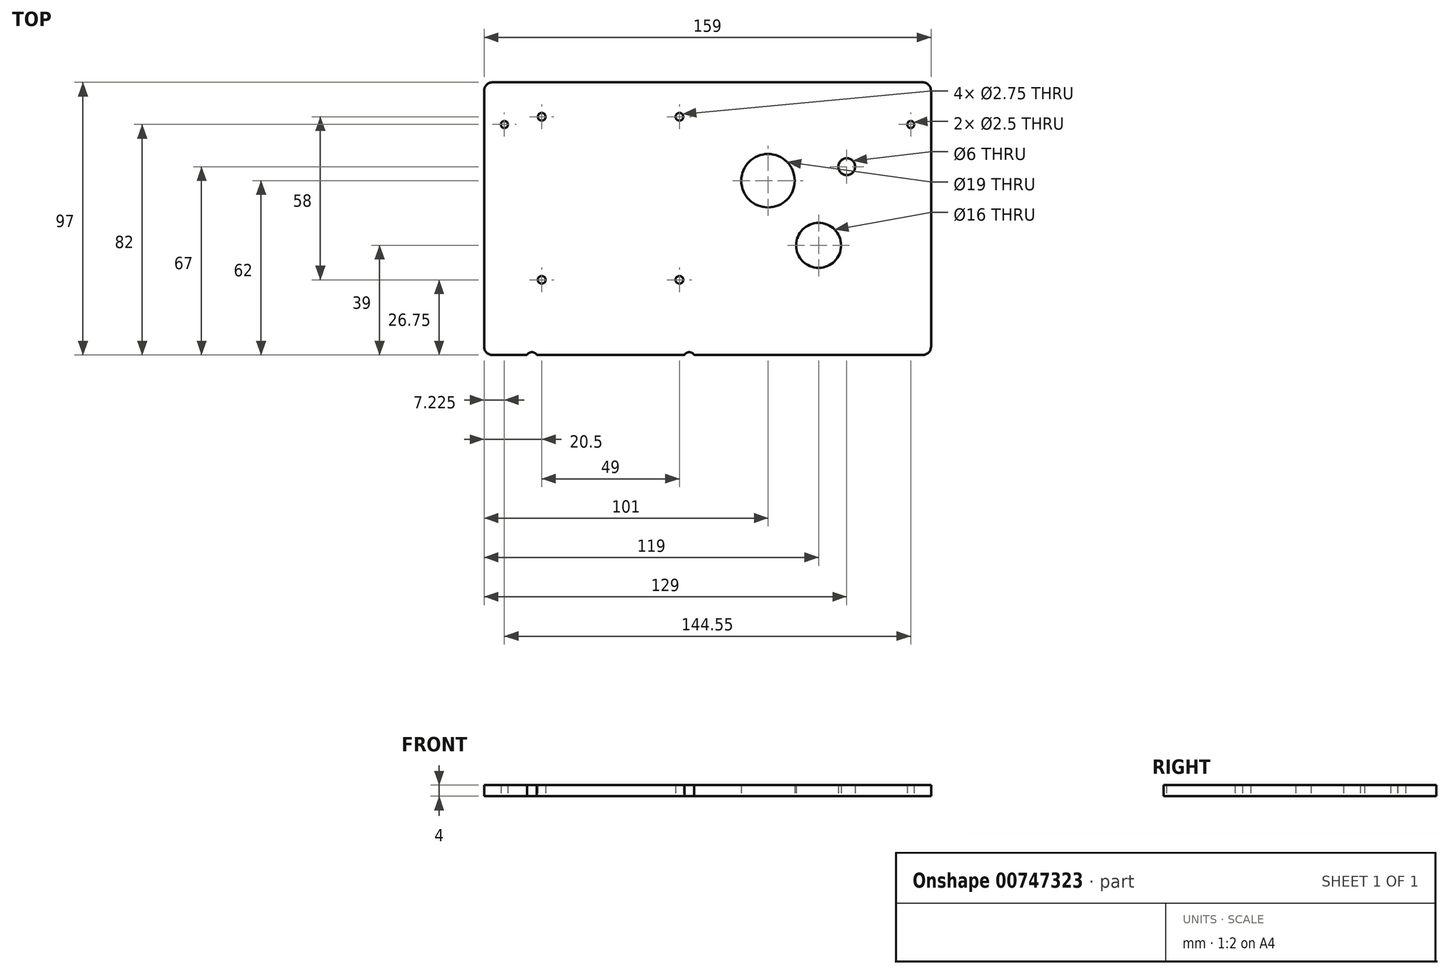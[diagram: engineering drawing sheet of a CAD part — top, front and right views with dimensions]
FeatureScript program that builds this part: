
annotation { "Feature Type Name" : "Feature", "Feature Type Description" : "" }
export const myFeature = defineFeature(function(context is Context, id is Id, definition is map)
    precondition{}
    {
        {
            var Q0;
            Q0=qCreatedBy(makeId("Top.planeOp"),FACE);
            var sketch = newSketch(context, id + "F0", { "sketchPlane" : qUnion([Q0])});
            skLineSegment(sketch, "E0.bottom", {"start": v(79.5, -48.5) * mm, "end": v(-79.5, -48.5) * mm});
            skLineSegment(sketch, "E0.top", {"start": v(79.5, 48.5) * mm, "end": v(-79.5, 48.5) * mm});
            skLineSegment(sketch, "E0.left", {"start": v(79.5, -48.5) * mm, "end": v(79.5, 48.5) * mm});
            skLineSegment(sketch, "E0.right", {"start": v(-79.5, -48.5) * mm, "end": v(-79.5, 48.5) * mm});
            skPoint(sketch, "E0.middle", {"position": v(0, 0) * mm});
            skLineSegment(sketch, "E1.bottom", {"start": v(-79.5, -48.5) * mm, "end": v(79.5, -48.5) * mm});
            skLineSegment(sketch, "E1.top", {"start": v(-79.5, -90.5) * mm, "end": v(79.5, -90.5) * mm});
            skLineSegment(sketch, "E1.left", {"start": v(-79.5, -48.5) * mm, "end": v(-79.5, -90.5) * mm});
            skLineSegment(sketch, "E1.right", {"start": v(79.5, -48.5) * mm, "end": v(79.5, -90.5) * mm});
            skLineSegment(sketch, "E2.bottom", {"start": v(-79.5, 48.5) * mm, "end": v(-72.28, 48.5) * mm, "construction": true});
            skLineSegment(sketch, "E2.top", {"start": v(-79.5, 33.5) * mm, "end": v(-72.28, 33.5) * mm, "construction": true});
            skLineSegment(sketch, "E2.left", {"start": v(-79.5, 48.5) * mm, "end": v(-79.5, 33.5) * mm, "construction": true});
            skLineSegment(sketch, "E2.right", {"start": v(-72.28, 48.5) * mm, "end": v(-72.28, 33.5) * mm, "construction": true});
            skLineSegment(sketch, "E3.bottom", {"start": v(79.5, 48.5) * mm, "end": v(72.28, 48.5) * mm, "construction": true});
            skLineSegment(sketch, "E3.top", {"start": v(79.5, 33.5) * mm, "end": v(72.28, 33.5) * mm, "construction": true});
            skLineSegment(sketch, "E3.left", {"start": v(79.5, 48.5) * mm, "end": v(79.5, 33.5) * mm, "construction": true});
            skLineSegment(sketch, "E3.right", {"start": v(72.28, 48.5) * mm, "end": v(72.28, 33.5) * mm, "construction": true});
            skCircle(sketch, "E4", {"center": v(-72.28, 33.5) * mm, "radius": 1.25 * mm});
            skCircle(sketch, "E5", {"center": v(72.28, 33.5) * mm, "radius": 1.25 * mm});
            skLineSegment(sketch, "E6.bottom", {"start": v(-62.5, -90.5) * mm, "end": v(-6.5, -90.5) * mm});
            skLineSegment(sketch, "E6.top", {"start": v(-62.5, -49.5) * mm, "end": v(-6.5, -49.5) * mm});
            skLineSegment(sketch, "E6.left", {"start": v(-62.5, -90.5) * mm, "end": v(-62.5, -49.5) * mm});
            skLineSegment(sketch, "E6.right", {"start": v(-6.5, -90.5) * mm, "end": v(-6.5, -49.5) * mm});
            skCircle(sketch, "E7", {"center": v(-62.5, -49.5) * mm, "radius": 2 * mm});
            skCircle(sketch, "E8", {"center": v(-6.5, -49.5) * mm, "radius": 2 * mm});
            skLineSegment(sketch, "E9.bottom", {"start": v(-79.5, -90.5) * mm, "end": v(-72.4, -90.5) * mm, "construction": true});
            skLineSegment(sketch, "E9.top", {"start": v(-79.5, -63.95) * mm, "end": v(-72.4, -63.95) * mm, "construction": true});
            skLineSegment(sketch, "E9.left", {"start": v(-79.5, -90.5) * mm, "end": v(-79.5, -63.95) * mm, "construction": true});
            skLineSegment(sketch, "E9.right", {"start": v(-72.4, -90.5) * mm, "end": v(-72.4, -63.95) * mm, "construction": true});
            skLineSegment(sketch, "E10.bottom", {"start": v(79.5, -90.5) * mm, "end": v(72.4, -90.5) * mm, "construction": true});
            skLineSegment(sketch, "E10.top", {"start": v(79.5, -63.95) * mm, "end": v(72.4, -63.95) * mm, "construction": true});
            skLineSegment(sketch, "E10.left", {"start": v(79.5, -90.5) * mm, "end": v(79.5, -63.95) * mm, "construction": true});
            skLineSegment(sketch, "E10.right", {"start": v(72.4, -90.5) * mm, "end": v(72.4, -63.95) * mm, "construction": true});
            skCircle(sketch, "E11", {"center": v(-72.4, -63.95) * mm, "radius": 1.25 * mm});
            skCircle(sketch, "E12", {"center": v(72.4, -63.95) * mm, "radius": 1.25 * mm});
            skLineSegment(sketch, "E13.bottom", {"start": v(-79.5, 48.5) * mm, "end": v(-62.5, 48.5) * mm, "construction": true});
            skLineSegment(sketch, "E13.top", {"start": v(-79.5, 39.75) * mm, "end": v(-62.5, 39.75) * mm, "construction": true});
            skLineSegment(sketch, "E13.left", {"start": v(-79.5, 48.5) * mm, "end": v(-79.5, 39.75) * mm, "construction": true});
            skLineSegment(sketch, "E13.right", {"start": v(-62.5, 48.5) * mm, "end": v(-62.5, 39.75) * mm, "construction": true});
            skLineSegment(sketch, "E14.bottom", {"start": v(-62.5, 39.75) * mm, "end": v(-6.5, 39.75) * mm, "construction": true});
            skLineSegment(sketch, "E14.top", {"start": v(-62.5, -45.25) * mm, "end": v(-6.5, -45.25) * mm, "construction": true});
            skLineSegment(sketch, "E14.left", {"start": v(-62.5, 39.75) * mm, "end": v(-62.5, -45.25) * mm, "construction": true});
            skLineSegment(sketch, "E14.right", {"start": v(-6.5, 39.75) * mm, "end": v(-6.5, -45.25) * mm, "construction": true});
            skLineSegment(sketch, "E15.bottom", {"start": v(-62.5, 39.75) * mm, "end": v(-59, 39.75) * mm, "construction": true});
            skLineSegment(sketch, "E15.top", {"start": v(-62.5, 36.25) * mm, "end": v(-59, 36.25) * mm, "construction": true});
            skLineSegment(sketch, "E15.left", {"start": v(-62.5, 39.75) * mm, "end": v(-62.5, 36.25) * mm, "construction": true});
            skLineSegment(sketch, "E15.right", {"start": v(-59, 39.75) * mm, "end": v(-59, 36.25) * mm, "construction": true});
            skLineSegment(sketch, "E16.bottom", {"start": v(-59, 36.25) * mm, "end": v(-10, 36.25) * mm, "construction": true});
            skLineSegment(sketch, "E16.top", {"start": v(-59, -21.75) * mm, "end": v(-10, -21.75) * mm, "construction": true});
            skLineSegment(sketch, "E16.left", {"start": v(-59, 36.25) * mm, "end": v(-59, -21.75) * mm, "construction": true});
            skLineSegment(sketch, "E16.right", {"start": v(-10, 36.25) * mm, "end": v(-10, -21.75) * mm, "construction": true});
            skCircle(sketch, "E17", {"center": v(-59, 36.25) * mm, "radius": 1.38 * mm});
            skCircle(sketch, "E18", {"center": v(-10, 36.25) * mm, "radius": 1.38 * mm});
            skCircle(sketch, "E19", {"center": v(-10, -21.75) * mm, "radius": 1.38 * mm});
            skCircle(sketch, "E20", {"center": v(-59, -21.75) * mm, "radius": 1.38 * mm});
            skLineSegment(sketch, "E21.bottom", {"start": v(79.5, 48.5) * mm, "end": v(21.5, 48.5) * mm, "construction": true});
            skLineSegment(sketch, "E21.top", {"start": v(79.5, 13.5) * mm, "end": v(21.5, 13.5) * mm, "construction": true});
            skLineSegment(sketch, "E21.left", {"start": v(79.5, 48.5) * mm, "end": v(79.5, 13.5) * mm, "construction": true});
            skLineSegment(sketch, "E21.right", {"start": v(21.5, 48.5) * mm, "end": v(21.5, 13.5) * mm, "construction": true});
            skLineSegment(sketch, "E22.bottom", {"start": v(79.5, 48.5) * mm, "end": v(49.5, 48.5) * mm, "construction": true});
            skLineSegment(sketch, "E22.top", {"start": v(79.5, 18.5) * mm, "end": v(49.5, 18.5) * mm, "construction": true});
            skLineSegment(sketch, "E22.left", {"start": v(79.5, 48.5) * mm, "end": v(79.5, 18.5) * mm, "construction": true});
            skLineSegment(sketch, "E22.right", {"start": v(49.5, 48.5) * mm, "end": v(49.5, 18.5) * mm, "construction": true});
            skLineSegment(sketch, "E23.bottom", {"start": v(79.5, 48.5) * mm, "end": v(39.5, 48.5) * mm, "construction": true});
            skLineSegment(sketch, "E23.top", {"start": v(79.5, -9.5) * mm, "end": v(39.5, -9.5) * mm, "construction": true});
            skLineSegment(sketch, "E23.left", {"start": v(79.5, 48.5) * mm, "end": v(79.5, -9.5) * mm, "construction": true});
            skLineSegment(sketch, "E23.right", {"start": v(39.5, 48.5) * mm, "end": v(39.5, -9.5) * mm, "construction": true});
            skCircle(sketch, "E24", {"center": v(21.5, 13.5) * mm, "radius": 9.5 * mm});
            skCircle(sketch, "E25", {"center": v(49.5, 18.5) * mm, "radius": 3 * mm});
            skCircle(sketch, "E26", {"center": v(39.5, -9.5) * mm, "radius": 8 * mm});
            skLineSegment(sketch, "E27", {"start": v(21.5, 13.5) * mm, "end": v(39.5, -9.5) * mm, "construction": true});
            skSolve(sketch);
        }
        {
            var Q0;
            Q0=makeQuery(id+"F0.imprint","IMPRINT",FACE,{"disambiguationData":[TD([[makeQuery(id+"F0.imprint","IMPRINT",EDGE,{"derivedFrom":sQuery(id+"F0.wireOp",EDGE,"E0.top")}),1.0]])]});
            var Q1;
            {var subQ0=sQuery(id+"F0.wireOp",EDGE,"E7");var subQ1=sQuery(id+"F0.wireOp",EDGE,"E1.bottom");var subQ2=makeQuery(id+"F0.imprint","INTERSECT",VERTEX,{"disambiguationData":[OD(0.0)],"derivedFrom":[subQ1,subQ0]});Q1=makeQuery(id+"F0.imprint","IMPRINT",FACE,{"disambiguationData":[TD([[makeQuery(id+"F0.imprint","IMPRINT",EDGE,{"disambiguationData":[TD([[subQ2,-1.0]])],"derivedFrom":subQ1}),1.0]])]});}
            var Q2;
            {var subQ0=sQuery(id+"F0.wireOp",EDGE,"E8");var subQ1=sQuery(id+"F0.wireOp",EDGE,"E1.bottom");var subQ2=makeQuery(id+"F0.imprint","INTERSECT",VERTEX,{"disambiguationData":[OD(0.0)],"derivedFrom":[subQ1,subQ0]});Q2=makeQuery(id+"F0.imprint","IMPRINT",FACE,{"disambiguationData":[TD([[makeQuery(id+"F0.imprint","IMPRINT",EDGE,{"disambiguationData":[TD([[subQ2,-1.0]])],"derivedFrom":subQ1}),1.0]])]});}
            extrude(context, id + "F1", {"entities" : qUnion([Q0, Q1, Q2]), "depth" : 4 * mm, "offsetDistance" : 25 * mm});
        }
        {
            var Q0;
            Q0=makeQuery(id+"F1.opExtrude","SWEPT_EDGE",EDGE,{"disambiguationData":[OSD([sQuery(id+"F0.wireOp",EDGE,"E1.top"),sQuery(id+"F0.wireOp",EDGE,"E1.right")])]});
            var Q1;
            Q1=makeQuery(id+"F1.opExtrude","SWEPT_EDGE",EDGE,{"disambiguationData":[OSD([sQuery(id+"F0.wireOp",EDGE,"E1.top"),sQuery(id+"F0.wireOp",EDGE,"E6.bottom"),sQuery(id+"F0.wireOp",EDGE,"E6.right")])]});
            var Q2;
            Q2=makeQuery(id+"F1.opExtrude","SWEPT_EDGE",EDGE,{"disambiguationData":[OSD([sQuery(id+"F0.wireOp",EDGE,"E1.top"),sQuery(id+"F0.wireOp",EDGE,"E6.bottom"),sQuery(id+"F0.wireOp",EDGE,"E6.left")])]});
            var Q3;
            Q3=makeQuery(id+"F1.opExtrude","SWEPT_EDGE",EDGE,{"disambiguationData":[OSD([sQuery(id+"F0.wireOp",EDGE,"E1.top"),sQuery(id+"F0.wireOp",EDGE,"E1.left")])]});
            var Q4;
            Q4=makeQuery(id+"F1.opExtrude","SWEPT_EDGE",EDGE,{"disambiguationData":[OSD([sQuery(id+"F0.wireOp",EDGE,"E0.top"),sQuery(id+"F0.wireOp",EDGE,"E0.right")])]});
            var Q5;
            Q5=makeQuery(id+"F1.opExtrude","SWEPT_EDGE",EDGE,{"disambiguationData":[OSD([sQuery(id+"F0.wireOp",EDGE,"E0.top"),sQuery(id+"F0.wireOp",EDGE,"E0.left")])]});
            fillet(context, id + "F2", {"entities" : qUnion([Q0, Q1, Q2, Q3, Q4, Q5]), "radius" : 3 * mm, "tangentPropagation" : true, "allowEdgeOverflow" : false});
        }
    });
